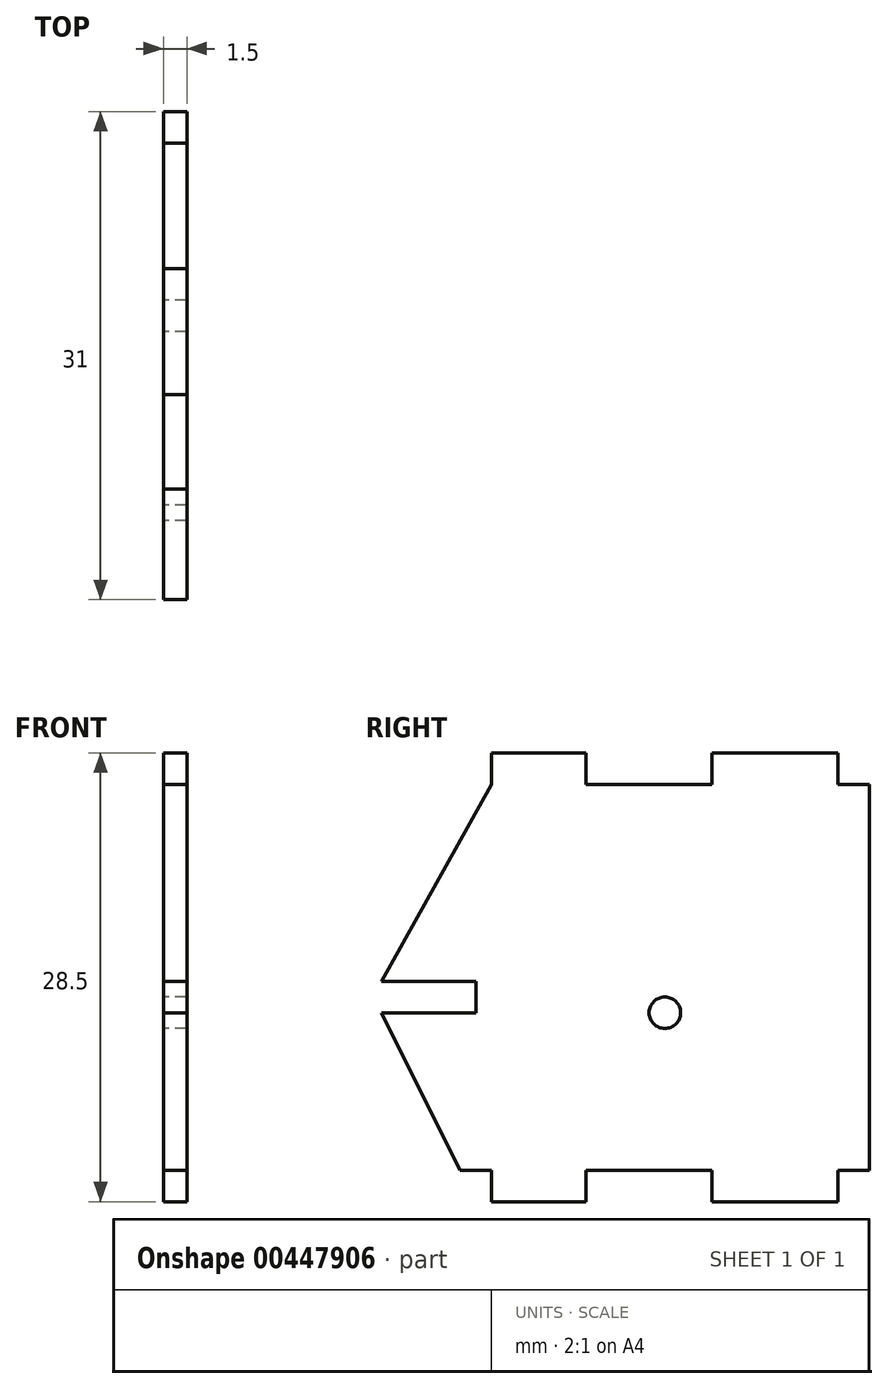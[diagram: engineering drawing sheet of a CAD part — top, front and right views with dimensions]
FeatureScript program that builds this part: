
annotation { "Feature Type Name" : "Feature", "Feature Type Description" : "" }
export const myFeature = defineFeature(function(context is Context, id is Id, definition is map)
    precondition{}
    {
        {
            var Q0;
            Q0=qCreatedBy(makeId("Right.planeOp"),FACE);
            var sketch = newSketch(context, id + "F0", { "sketchPlane" : qUnion([Q0])});
            skLineSegment(sketch, "E0", {"start": v(0, 0) * mm, "end": v(-2, 0) * mm});
            skLineSegment(sketch, "E1", {"start": v(-2, 0) * mm, "end": v(-2, -2) * mm});
            skLineSegment(sketch, "E2", {"start": v(-2, -2) * mm, "end": v(-10, -2) * mm});
            skLineSegment(sketch, "E3", {"start": v(-10, -2) * mm, "end": v(-10, 0) * mm});
            skLineSegment(sketch, "E4", {"start": v(-10, 0) * mm, "end": v(-18, 0) * mm});
            skLineSegment(sketch, "E5", {"start": v(-18, 0) * mm, "end": v(-18, -2) * mm});
            skLineSegment(sketch, "E6", {"start": v(-18, -2) * mm, "end": v(-24, -2) * mm});
            skLineSegment(sketch, "E7", {"start": v(-24, -2) * mm, "end": v(-24, 0) * mm});
            skLineSegment(sketch, "E8", {"start": v(-24, 0) * mm, "end": v(-26, 0) * mm});
            skLineSegment(sketch, "E9", {"start": v(-26, 0) * mm, "end": v(-31, 10) * mm});
            skLineSegment(sketch, "E10", {"start": v(-31, 10) * mm, "end": v(-25, 10) * mm});
            skLineSegment(sketch, "E11", {"start": v(-25, 10) * mm, "end": v(-25, 12) * mm});
            skLineSegment(sketch, "E12", {"start": v(-25, 12) * mm, "end": v(-31, 12) * mm});
            skLineSegment(sketch, "E13", {"start": v(-24, 26.5) * mm, "end": v(-18, 26.5) * mm});
            skLineSegment(sketch, "E14", {"start": v(-18, 26.5) * mm, "end": v(-18, 24.5) * mm});
            skLineSegment(sketch, "E15", {"start": v(-18, 24.5) * mm, "end": v(-10, 24.5) * mm});
            skLineSegment(sketch, "E16", {"start": v(-10, 24.5) * mm, "end": v(-10, 26.5) * mm});
            skLineSegment(sketch, "E17", {"start": v(-10, 26.5) * mm, "end": v(-2, 26.5) * mm});
            skLineSegment(sketch, "E18", {"start": v(-2, 26.5) * mm, "end": v(-2, 24.5) * mm});
            skLineSegment(sketch, "E19", {"start": v(-2, 24.5) * mm, "end": v(0, 24.5) * mm});
            skLineSegment(sketch, "E20", {"start": v(0, 24.5) * mm, "end": v(0, 0) * mm});
            skCircle(sketch, "E21", {"center": v(-13, 10) * mm, "radius": 1 * mm});
            skLineSegment(sketch, "E22", {"start": v(-24, 26.5) * mm, "end": v(-24, 24.5) * mm});
            skLineSegment(sketch, "E23", {"start": v(-24, 24.5) * mm, "end": v(-31, 12) * mm});
            skSolve(sketch);
        }
        {
            var Q0;
            Q0 = qSketchRegion(id + "F0", true);
            extrude(context, id + "F1", {"entities" : qUnion([Q0]), "depth" : 1.5 * mm});
        }
    });
